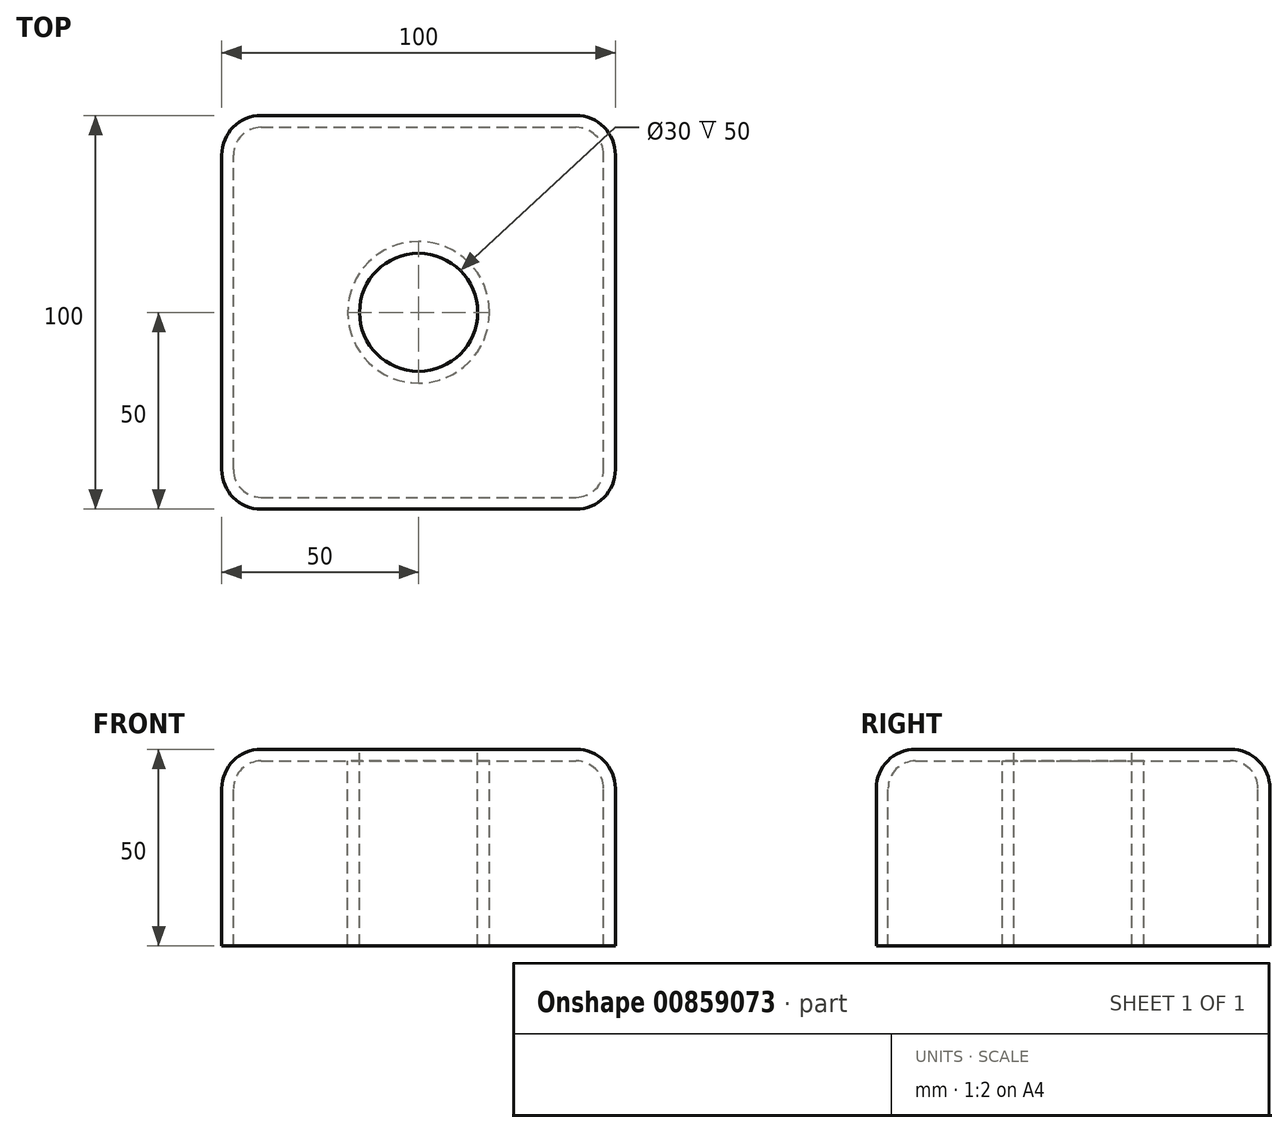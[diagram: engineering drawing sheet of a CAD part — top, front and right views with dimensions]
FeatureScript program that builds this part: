
annotation { "Feature Type Name" : "Feature", "Feature Type Description" : "" }
export const myFeature = defineFeature(function(context is Context, id is Id, definition is map)
    precondition{}
    {
        {
            var Q0;
            Q0=qCreatedBy(makeId("Front.planeOp"),FACE);
            var sketch = newSketch(context, id + "F0", { "sketchPlane" : qUnion([Q0])});
            skLineSegment(sketch, "E0.bottom", {"start": v(0, 0) * mm, "end": v(100, 0) * mm});
            skLineSegment(sketch, "E0.top", {"start": v(0, 50) * mm, "end": v(100, 50) * mm});
            skLineSegment(sketch, "E0.left", {"start": v(0, 0) * mm, "end": v(0, 50) * mm});
            skLineSegment(sketch, "E0.right", {"start": v(100, 0) * mm, "end": v(100, 50) * mm});
            skSolve(sketch);
        }
        {
            var Q0;
            Q0 = qSketchRegion(id + "F0", true);
            extrude(context, id + "F1", {"entities" : qUnion([Q0]), "depth" : 100 * mm, "offsetDistance" : 25.4 * mm});
        }
        {
            var Q0;
            Q0=makeQuery(id+"F1.opExtrude","SWEPT_FACE",FACE,{"disambiguationData":[OSD([sQuery(id+"F0.wireOp",EDGE,"E0.top")])]});
            var sketch = newSketch(context, id + "F2", { "sketchPlane" : qUnion([Q0])});
            skCircle(sketch, "E1", {"center": v(50, -50) * mm, "radius": 15 * mm});
            skSolve(sketch);
        }
        {
            var Q0;
            Q0 = qSketchRegion(id + "F2", true);
            var Q1;
            Q1=makeQuery(id+"F1.opExtrude","SWEPT_FACE",FACE,{"disambiguationData":[OSD([sQuery(id+"F0.wireOp",EDGE,"E0.bottom")])]});
            extrude(context, id + "F3", {"entities" : qUnion([Q0]), "operationType" : NewBodyOperationType.REMOVE, "endBound" : BoundingType.UP_TO_SURFACE, "oppositeDirection" : true, "depth" : 25 * mm, "endBoundEntityFace" : qUnion([Q1]), "offsetDistance" : 25 * mm});
        }
        {
            var Q0;
            Q0=makeQuery(id+"F1.opExtrude","CAP_EDGE",EDGE,{"disambiguationData":[OSD([sQuery(id+"F0.wireOp",EDGE,"E0.right")])],"isStart":true});
            var Q1;
            Q1=makeQuery(id+"F1.opExtrude","CAP_EDGE",EDGE,{"disambiguationData":[OSD([sQuery(id+"F0.wireOp",EDGE,"E0.left")])],"isStart":true});
            var Q2;
            Q2=makeQuery(id+"F1.opExtrude","CAP_EDGE",EDGE,{"disambiguationData":[OSD([sQuery(id+"F0.wireOp",EDGE,"E0.right")])],"isStart":false});
            var Q3;
            Q3=makeQuery(id+"F1.opExtrude","CAP_EDGE",EDGE,{"disambiguationData":[OSD([sQuery(id+"F0.wireOp",EDGE,"E0.left")])],"isStart":false});
            var Q4;
            Q4=makeQuery(id+"F1.opExtrude","CAP_EDGE",EDGE,{"disambiguationData":[OSD([sQuery(id+"F0.wireOp",EDGE,"E0.top")])],"isStart":false});
            var Q5;
            Q5=makeQuery(id+"F1.opExtrude","SWEPT_EDGE",EDGE,{"disambiguationData":[OSD([sQuery(id+"F0.wireOp",EDGE,"E0.top"),sQuery(id+"F0.wireOp",EDGE,"E0.left")])]});
            var Q6;
            Q6=makeQuery(id+"F1.opExtrude","SWEPT_EDGE",EDGE,{"disambiguationData":[OSD([sQuery(id+"F0.wireOp",EDGE,"E0.top"),sQuery(id+"F0.wireOp",EDGE,"E0.right")])]});
            var Q7;
            Q7=makeQuery(id+"F1.opExtrude","CAP_EDGE",EDGE,{"disambiguationData":[OSD([sQuery(id+"F0.wireOp",EDGE,"E0.top")])],"isStart":true});
            fillet(context, id + "F4", {"entities" : qUnion([Q0, Q1, Q2, Q3, Q4, Q5, Q6, Q7]), "radius" : 10 * mm, "tangentPropagation" : true, "allowEdgeOverflow" : false});
        }
        {
            var Q0;
            Q0=makeQuery(id+"F1.opExtrude","SWEPT_FACE",FACE,{"disambiguationData":[OSD([sQuery(id+"F0.wireOp",EDGE,"E0.bottom")])]});
            shell(context, id + "F5", {"entities" : qUnion([Q0]), "thickness" : 3 * mm});
        }
    });
